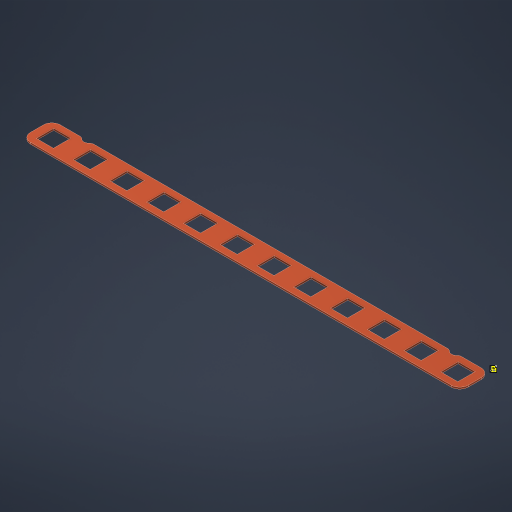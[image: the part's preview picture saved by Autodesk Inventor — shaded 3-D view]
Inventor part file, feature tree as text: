
AUTODESK INVENTOR PART (.ipt)
format: ipt  version: 2024.3 (Build 283343010, 343A)  size: 349,184 bytes
history: native  units: mm
features: fillet x2, sketch x2, extrude x1, projected_geometry x1
ambient origin geometry x8: Origin, YZ Plane, XZ Plane, XY Plane, X Axis, Y Axis, Z Axis, Center Point
bodies: Volumenkörper1 (feature_tree)
feature tree (6):
  extrude  "Extrusion1"  Depth=17.5mm
  fillet  "Rundung1"  Radius=10.2mm
  fillet  "Rundung2"  Radius=10.0mm
  sketch  "Skizze2"  dims[d14=1.0mm d15=0.0mm d16=5.0mm d17=120.0mm d19=21.5mm d20=10.0mm d22=10.0mm d24=43.0mm d25=21.5mm d26=10.75mm d32=3.0mm d33=1.25mm d34=10.75mm d35=10.75mm d36=3.0mm]
  sketch  "Skizze1"  dims[d0=256.0mm d1=17.5mm d2=10.2mm d3=10.0mm]
  projected_geometry  "Projizierte Kontur1"
